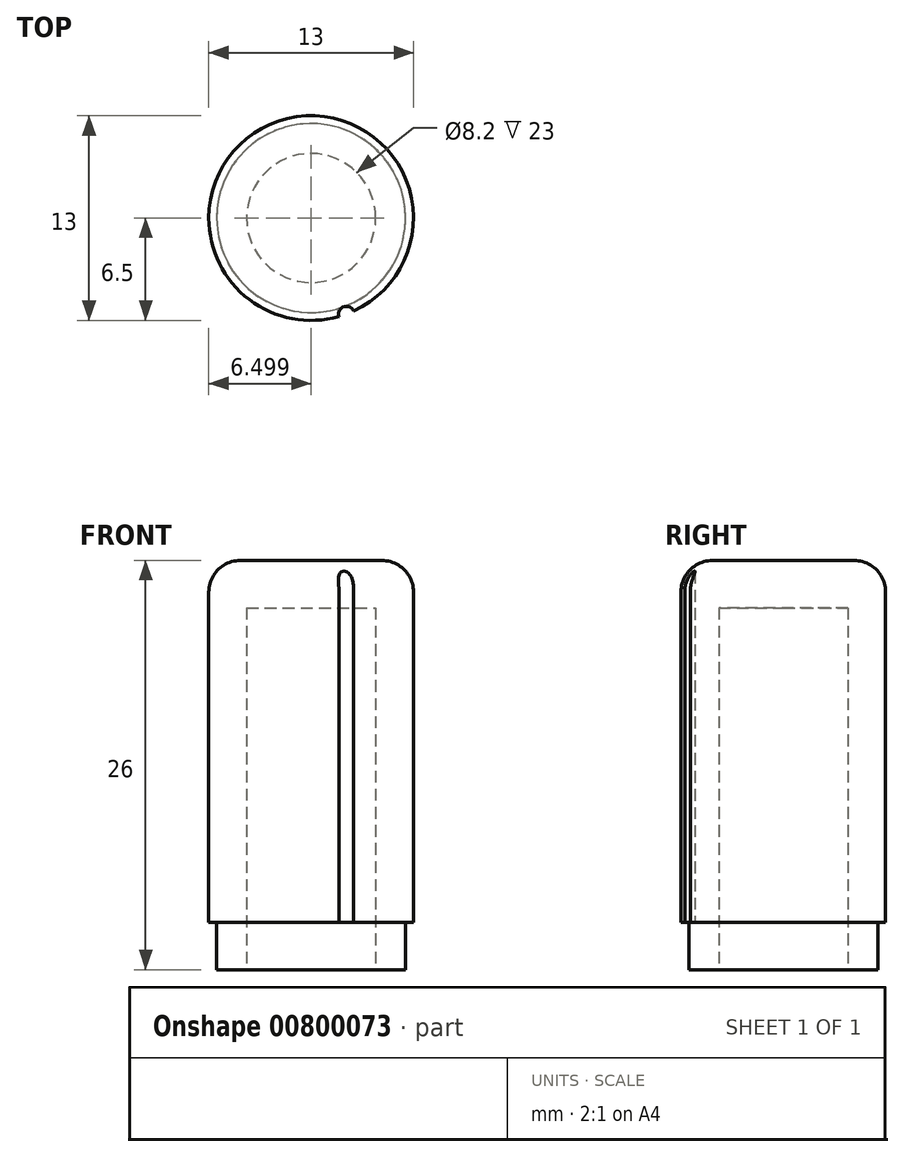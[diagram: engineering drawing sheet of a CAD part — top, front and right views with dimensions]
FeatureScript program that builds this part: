
annotation { "Feature Type Name" : "Feature", "Feature Type Description" : "" }
export const myFeature = defineFeature(function(context is Context, id is Id, definition is map)
    precondition{}
    {
        {
            var Q0;
            Q0=qCreatedBy(makeId("Front.planeOp"),FACE);
            var sketch = newSketch(context, id + "F0", { "sketchPlane" : qUnion([Q0])});
            skLineSegment(sketch, "E0", {"start": v(-27.02, 37.16) * mm, "end": v(-22.92, 37.16) * mm});
            skLineSegment(sketch, "E1", {"start": v(-22.92, 14.16) * mm, "end": v(-22.92, 37.16) * mm});
            skLineSegment(sketch, "E2", {"start": v(-27.02, 37.16) * mm, "end": v(-27.02, 40.16) * mm});
            skLineSegment(sketch, "E3", {"start": v(-27.02, 40.16) * mm, "end": v(-20.52, 40.16) * mm});
            skLineSegment(sketch, "E4", {"start": v(-20.52, 40.16) * mm, "end": v(-20.52, 17.16) * mm});
            skLineSegment(sketch, "E5", {"start": v(-20.52, 17.16) * mm, "end": v(-21.02, 17.16) * mm});
            skLineSegment(sketch, "E6", {"start": v(-21.02, 17.16) * mm, "end": v(-21.02, 14.16) * mm});
            skLineSegment(sketch, "E7", {"start": v(-21.02, 14.16) * mm, "end": v(-22.92, 14.16) * mm});
            skSolve(sketch);
        }
        {
            var Q0;
            Q0=makeQuery(id+"F0.imprint","IMPRINT",FACE,{"disambiguationData":[TD([[makeQuery(id+"F0.imprint","IMPRINT",EDGE,{"derivedFrom":sQuery(id+"F0.wireOp",EDGE,"E0")}),1.0]])]});
            var Q1;
            Q1=sQuery(id+"F0.wireOp",EDGE,"E2");
            revolve(context, id + "F1", {"surfaceOperationType" : NewSurfaceOperationType.NEW, "entities" : qUnion([Q0]), "axis" : qUnion([Q1]), "revolveType" : RevolveType.FULL});
        }
        {
            var Q0;
            Q0=makeQuery(id+"F1.opRevolve","SWEPT_EDGE",EDGE,{"disambiguationData":[OSD([sQuery(id+"F0.wireOp",EDGE,"E3"),sQuery(id+"F0.wireOp",EDGE,"E4")])]});
            fillet(context, id + "F2", {"entities" : qUnion([Q0]), "radius" : 2 * mm, "tangentPropagation" : true, "allowEdgeOverflow" : false});
        }
        {
            var Q0;
            Q0=makeQuery(id+"F1.opRevolve","SWEPT_FACE",FACE,{"disambiguationData":[OSD([sQuery(id+"F0.wireOp",EDGE,"E5")])]});
            var sketch = newSketch(context, id + "F3", { "sketchPlane" : qUnion([Q0])});
            skCircle(sketch, "E8", {"center": v(-24.78, 6.1) * mm, "radius": 0.5 * mm});
            skSolve(sketch);
        }
        {
            var Q0;
            {var subQ0=sQuery(id+"F3.wireOp",EDGE,"E8");var subQ1=sQuery(id+"F0.wireOp",EDGE,"E5");var subQ2=makeQuery(id+"F3.imprint","INTERSECT",VERTEX,{"derivedFrom":[makeQuery(id+"F1.opRevolve","SWEPT_EDGE",EDGE,{"disambiguationData":[OSD([subQ1,sQuery(id+"F0.wireOp",EDGE,"E6")])]}),subQ0]});Q0=makeQuery(id+"F3.imprint","IMPRINT",FACE,{"disambiguationData":[TD([[makeQuery(id+"F3.imprint","IMPRINT",EDGE,{"disambiguationData":[TD([[subQ2,1.0]])],"derivedFrom":subQ0}),1.0]])]});}
            extrude(context, id + "F4", {"entities" : qUnion([Q0]), "operationType" : NewBodyOperationType.REMOVE, "endBound" : BoundingType.UP_TO_NEXT, "oppositeDirection" : true, "depth" : 25 * mm, "offsetDistance" : 25 * mm});
        }
    });
